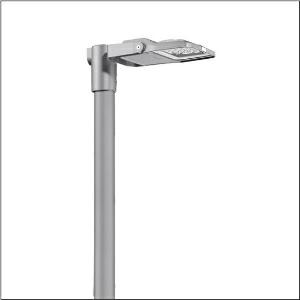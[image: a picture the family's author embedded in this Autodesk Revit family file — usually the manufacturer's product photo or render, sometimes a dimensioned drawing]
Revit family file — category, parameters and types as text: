
# Revit family: floodlight_fl_21_iq_micro___pl33t_5xa7762a4f3a_b73c
name_source: partatom
category: Lighting Fixtures
units: mm (PartAtom-declared; Revit-internal decimal feet)

## family parameters
Cut with Voids When Loaded = No
Host = Face
Light Source = No
Part Type = Normal
Room Calculation Point = No
Round Connector Dimension = Use Diameter
Shared = No

## types (1)
- --- (1 x LED, 3050 lm, 23.1 W, 4000K)
    Apparent Load = 23 VA
    CIE Flux Codes = 26 75 99 100 100
    Color Rendering = 70
    Color Temperature = 4000K
    Default Elevation = 1800 mm
    Description = Floodlight FL 21 iQ micro, floodlight, primary light control with lens, of PMMA, primary optical cover: protective disc, of toughened safety glass, transparent, light distribution: PL33T, light emission: direct distribution, installation type: surface-mounted, LED, High Power LED, rated luminous flux: 3.050lm, luminous efficacy: 132lm/W, light colour: 740, colour temperature: 4000K, control: Auto-Match, Temp-Guard, Night-Set, Smart-Wire, Desk-Remote (wireless, voltage-free reading and setting of iQ features in the workshop via application-optimized NFC function/RFID function), optimised constant luminous flux control (CLO 2.0), Street-Remote, with terminal, 6-pole, mains connection: 220..240V, AC, 50/60Hz, start of lifetime: 23W, end of service life: 24W, reduction: 11W, luminaire housing, of diecast aluminium, powder-coated, Siteco® metallic grey (DB 702S), corrosivity category C5 mid according to DIN EN ISO 12944, sealing non-destructively replaceable, please order mast flange separately, mast bracket, of steel, galvanised, powder-coated, Siteco® metallic grey (DB 702S), protection rating (complete): IP66, insulation class (complete): insulation class II (safety insulation), certification: CE, ENEC, VDE, protection symbol: D, impact resistance: IK07, permissible operating ambient temperature: -40..+40°C, permissible operating ambient temperature for outdoor applications: -40..+50°C, standard: DIN EN 12944, LABS conformity tested according to VDMA 24364:2018-05, packaging unit: 1 piece

Light Distribution: PL33T
    Height = 65 mm
    Lamp = 1 x LED
    Lamp Light Flux = 3050 lm
    Lamp Power = 23.1 W
    Lamp count = 1
    Length = 312 mm
    Luminous efficacy = 132 lm/W
    Manufacturer = Siteco
    ModVariant = No
    Model = 5XA7762A4F3A
    Number of Poles = 1
    OnlyDefault = Yes
    Power Factor = 1
    Product Name = Floodlight FL 21 iQ micro | PL33T
    Product group = floodlight | pylon annexe
    ProductGroupID = 6200
    Protection Class = Protection class II
    Protection Degree = IP 66
    RLX_Detail_Level = 1
    RLX_Emergency_Light_Flux = 0 lm
    RLX_Emergency_Type = 0
    RLX_Emergency_Type_DB = No
    RlxData = <blob elided: 101569 chars, md5=943a449d>
    Socket = socket
    Standby Power = 0 W
    System Light Flux = 3050 lm
    System Power = 23 W
    Type Comments = factory setting: luminous flux: 100 % | dim-lin: 254 | 455 mA
    Type Image = l_1007121.jpg
    URL = http://relux.com
    VarID = @adj_080349
    Voltage = 0 V
    Weight = 0.00 kg
    Width = 230 mm

## geometry (parser evidence)
native form markers: Blend x4, Sweep x11
no freeform markers — native parametric forms only
